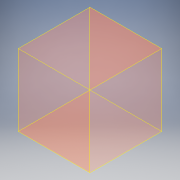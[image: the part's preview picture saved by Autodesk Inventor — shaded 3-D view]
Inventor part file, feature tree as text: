
AUTODESK INVENTOR PART (.ipt)
format: ipt  version: 2017 (Build 210142000, 142)  size: 97,280 bytes
history: native  units: in
note: dims shown in document units (in); Inventor stores cm internally (conversion verified against a paired STEP export)
features: sketch x1, other x1, extrude x1
ambient origin geometry x8: Origin, YZ Plane, XZ Plane, XY Plane, X Axis, Y Axis, Z Axis, Center Point
bodies: Body1 (feature_tree)
feature tree (3):
  sketch  "Sketch1"  dims[d0=18.0in d1=18.0in d4=18.0in d5=0.0in]
  other  "Srf1"
  extrude  "ExtrusionSrf1"  Depth=18.0in
